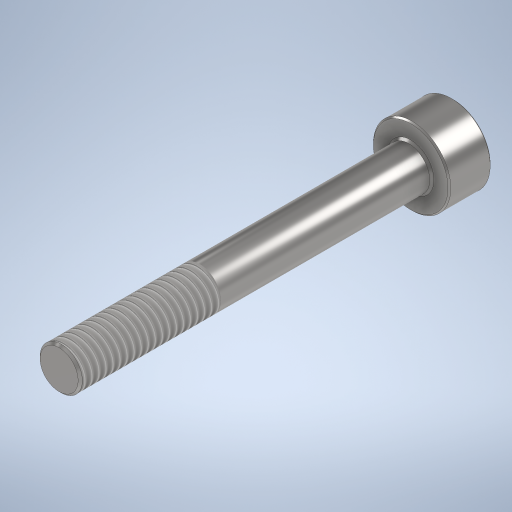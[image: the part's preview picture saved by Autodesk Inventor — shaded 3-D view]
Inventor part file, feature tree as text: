
AUTODESK INVENTOR PART (.ipt)
format: ipt  version: 2024 (Build 280153000, 153)  size: 329,728 bytes
history: native  units: mm
features: extrude x3, chamfer x3, sketch x2, thread x1, hole x1
ambient origin geometry x8: Origin, YZ Plane, XZ Plane, XY Plane, X Axis, Y Axis, Z Axis, Center Point
bodies: Solid1 (feature_tree)
feature tree (10):
  sketch  "Sketch1"  dims[d0=5.5mm d1=3.0mm]
  extrude  "Extrusion1"  Depth=3.0mm
  extrude  "Extrusion2"  Depth=1.5mm TaperAngle=0.0deg
  thread  "Thread1"  [1 undecoded]
  chamfer  "Chamfer1"  Distance=0.1mm Angle=45.0deg
  sketch  "Sketch2"  dims[d2=25.0mm d3=0.0mm d4=3.0mm d5=0.0mm d6=10.0mm d7=15.0mm d8=0.1mm d9=2.0mm d10=45.0deg d11=2.4mm d12=2.5mm d15=0.35mm d16=2.0mm d17=45.0deg d18=3.0mm d19=0.0mm d20=0.15mm d21=2.0mm d22=45.0deg d23=2.4mm d24=6.0mm d25=4.0mm d26=2.0mm d27=90.0deg d28=1.5mm d29=150.0deg]
  hole  "Hole1"  [1 undecoded]
  chamfer  "Chamfer2"  Distance=2.5mm
  extrude  "Extrusion4"  Depth=1.5mm TaperAngle=45.0deg
  chamfer  "Chamfer3"  Distance=3.0mm
note: 2 required parameter values undecoded (feature->parameter linkage not recoverable at this tier; creation-order binding heuristic only, values carry confidence <= 0.55)
